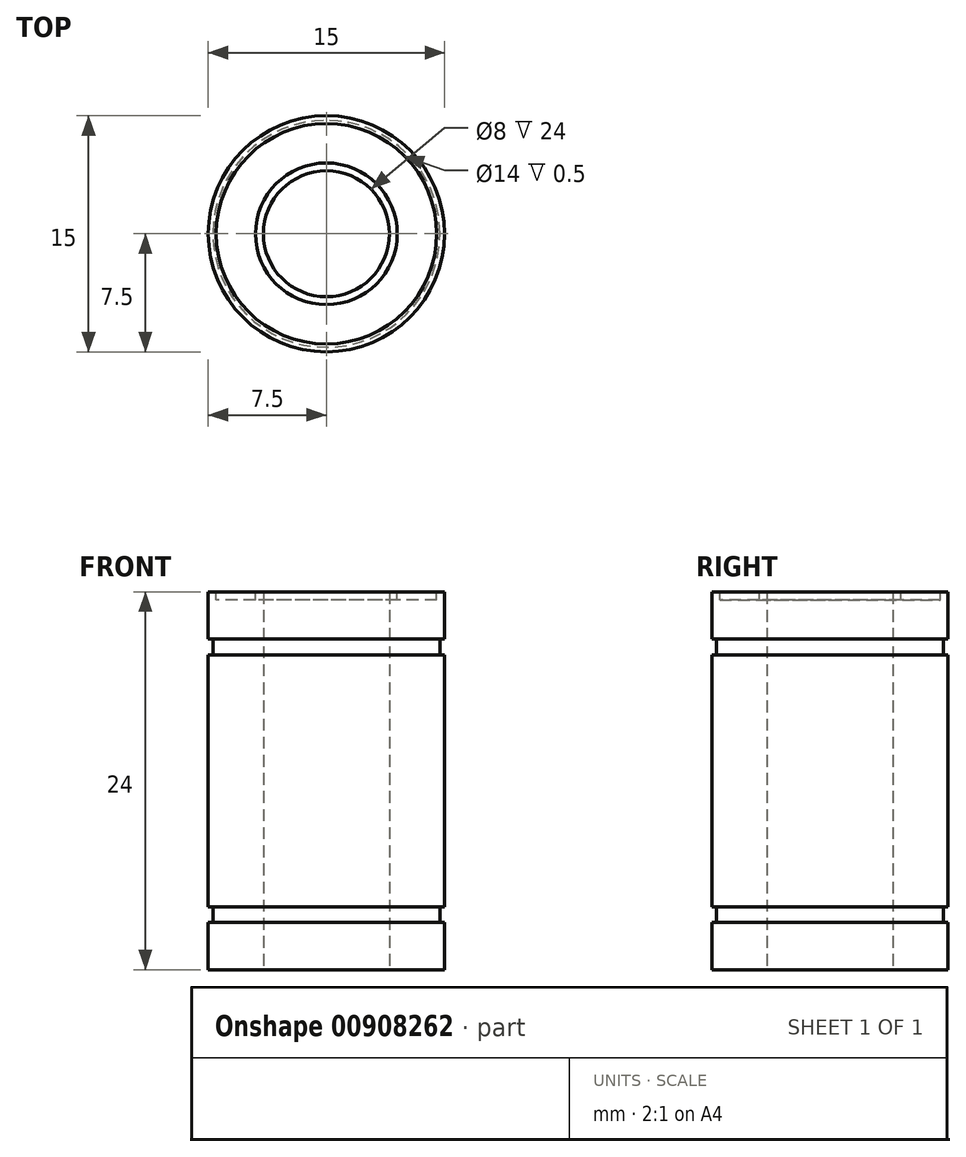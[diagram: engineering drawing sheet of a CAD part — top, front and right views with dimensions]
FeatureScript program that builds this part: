
annotation { "Feature Type Name" : "Feature", "Feature Type Description" : "" }
export const myFeature = defineFeature(function(context is Context, id is Id, definition is map)
    precondition{}
    {
        {
            var Q0;
            Q0=qCreatedBy(makeId("Top.planeOp"),FACE);
            var sketch = newSketch(context, id + "F0", { "sketchPlane" : qUnion([Q0])});
            skCircle(sketch, "E0", {"center": v(0, 0) * mm, "radius": 7.5 * mm});
            skCircle(sketch, "E1", {"center": v(0, 0) * mm, "radius": 4 * mm});
            skSolve(sketch);
        }
        {
            var Q0;
            Q0 = qSketchRegion(id + "F0", true);
            extrude(context, id + "F1", {"entities" : qUnion([Q0]), "depth" : 24 * mm, "offsetDistance" : 25 * mm});
        }
        {
            var Q0;
            Q0=qCreatedBy(makeId("Right.planeOp"),FACE);
            var sketch = newSketch(context, id + "F2", { "sketchPlane" : qUnion([Q0])});
            skLineSegment(sketch, "E2.bottom", {"start": v(9.8, 20) * mm, "end": v(7.2, 20) * mm});
            skLineSegment(sketch, "E2.top", {"start": v(9.8, 21) * mm, "end": v(7.2, 21) * mm});
            skLineSegment(sketch, "E2.left", {"start": v(9.8, 20) * mm, "end": v(9.8, 21) * mm});
            skLineSegment(sketch, "E2.right", {"start": v(7.2, 20) * mm, "end": v(7.2, 21) * mm});
            skPoint(sketch, "E2.middle", {"position": v(8.5, 20.5) * mm});
            skLineSegment(sketch, "E3.bottom", {"start": v(9.8, 3) * mm, "end": v(7.2, 3) * mm});
            skLineSegment(sketch, "E3.top", {"start": v(9.8, 4) * mm, "end": v(7.2, 4) * mm});
            skLineSegment(sketch, "E3.left", {"start": v(9.8, 3) * mm, "end": v(9.8, 4) * mm});
            skLineSegment(sketch, "E3.right", {"start": v(7.2, 3) * mm, "end": v(7.2, 4) * mm});
            skPoint(sketch, "E3.middle", {"position": v(8.5, 3.5) * mm});
            skSolve(sketch);
        }
        {
            var Q0;
            Q0 = qSketchRegion(id + "F2", true);
            var Q1;
            Q1=makeQuery(id+"F1.opExtrude","CAP_EDGE",EDGE,{"disambiguationData":[OSD([sQuery(id+"F0.wireOp",EDGE,"E1")])],"isStart":false});
            revolve(context, id + "F3", {"operationType" : NewBodyOperationType.REMOVE, "surfaceOperationType" : NewSurfaceOperationType.NEW, "entities" : qUnion([Q0]), "axis" : qUnion([Q1]), "revolveType" : RevolveType.FULL, "oppositeDirection" : true});
        }
        {
            var Q0;
            Q0=makeQuery(id+"F1.opExtrude","CAP_FACE",FACE,{"disambiguationData":[OSD([sQuery(id+"F0.wireOp",EDGE,"E0"),sQuery(id+"F0.wireOp",EDGE,"E1")])],"isStart":false});
            var sketch = newSketch(context, id + "F4", { "sketchPlane" : qUnion([Q0])});
            skCircle(sketch, "E4", {"center": v(0, 0) * mm, "radius": 7 * mm});
            skCircle(sketch, "E5", {"center": v(0, 0) * mm, "radius": 4.5 * mm});
            skSolve(sketch);
        }
        {
            var Q0;
            Q0=makeQuery(id+"F4.imprint","IMPRINT",FACE,{"disambiguationData":[TD([[makeQuery(id+"F4.imprint","IMPRINT",EDGE,{"derivedFrom":sQuery(id+"F4.wireOp",EDGE,"E4")}),1.0]])]});
            extrude(context, id + "F5", {"entities" : qUnion([Q0]), "operationType" : NewBodyOperationType.REMOVE, "oppositeDirection" : true, "depth" : 0.5 * mm, "offsetDistance" : 25 * mm});
        }
        {
            var Q0;
            Q0=qCreatedBy(makeId("Top.planeOp"),FACE);
            cPlane(context, id + "F6", {"entities" : qUnion([Q0]), "cplaneType" : CPlaneType.OFFSET, "offset" : 12 * mm, "width" : 150 * mm, "height" : 150 * mm});
        }
    });
